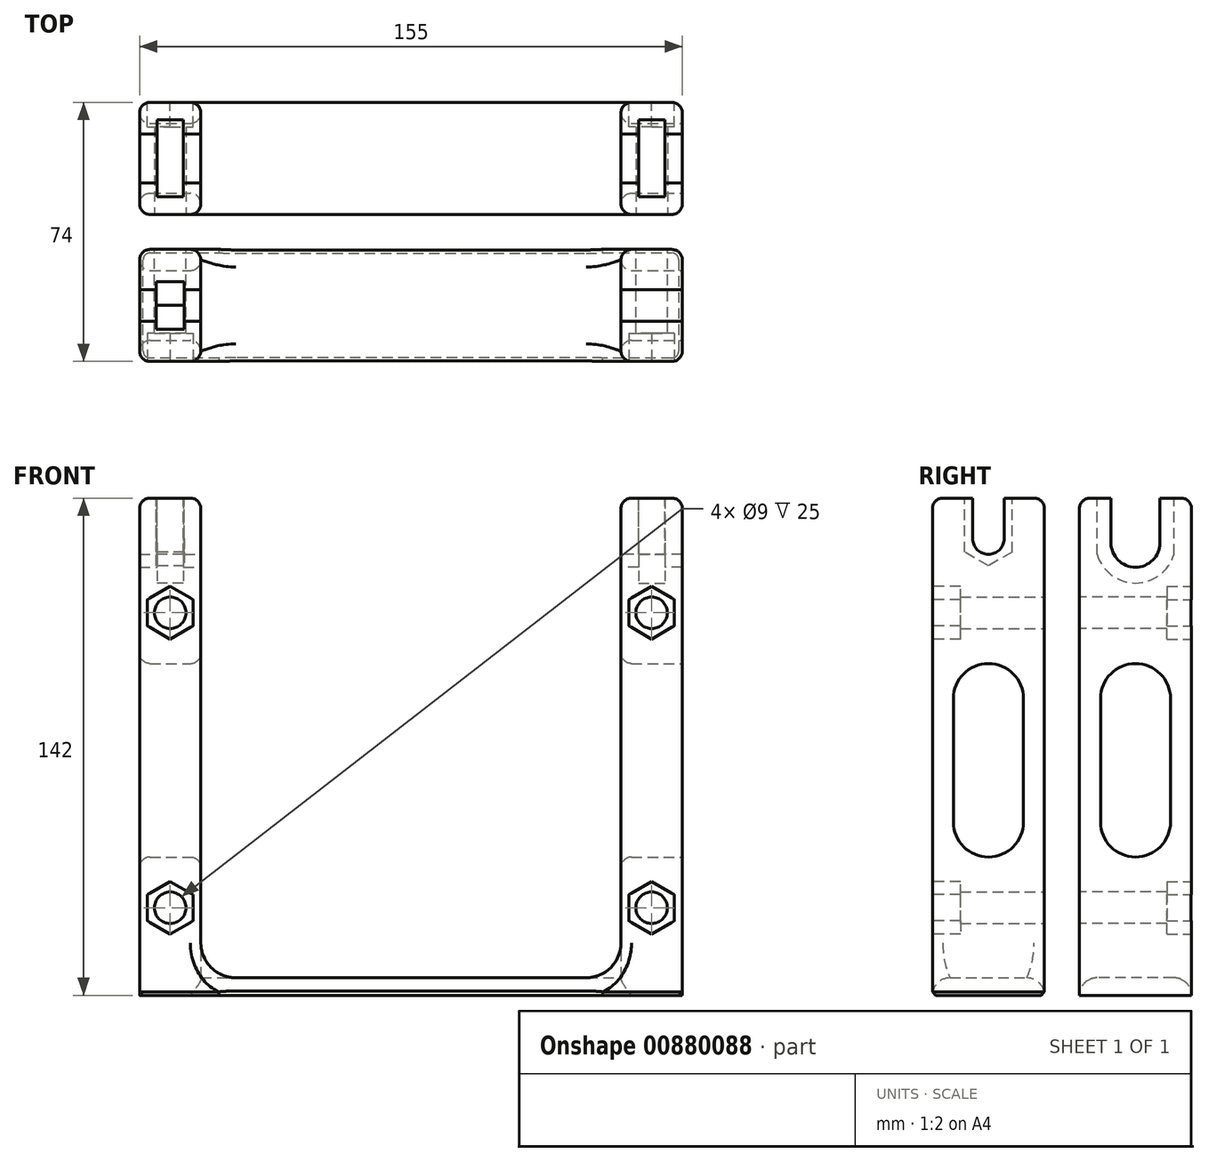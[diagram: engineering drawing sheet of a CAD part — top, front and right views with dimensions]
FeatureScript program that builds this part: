
annotation { "Feature Type Name" : "Feature", "Feature Type Description" : "" }
export const myFeature = defineFeature(function(context is Context, id is Id, definition is map)
    precondition{}
    {
        {
            var Q0;
            Q0=qCreatedBy(makeId("Top.planeOp"),FACE);
            var sketch = newSketch(context, id + "F0", { "sketchPlane" : qUnion([Q0])});
            skLineSegment(sketch, "E0.bottom", {"start": v(-77.5, 16) * mm, "end": v(-60, 16) * mm});
            skLineSegment(sketch, "E0.top", {"start": v(-77.5, -16) * mm, "end": v(-60, -16) * mm});
            skLineSegment(sketch, "E0.left", {"start": v(-77.5, 16) * mm, "end": v(-77.5, -16) * mm});
            skLineSegment(sketch, "E0.right", {"start": v(-60, 16) * mm, "end": v(-60, -16) * mm});
            skPoint(sketch, "E1", {"position": v(-60, 0) * mm});
            skSolve(sketch);
        }
        {
            var Q0;
            Q0=makeQuery(id+"F0.imprint","IMPRINT",FACE,{"disambiguationData":[TD([[makeQuery(id+"F0.imprint","IMPRINT",EDGE,{"derivedFrom":sQuery(id+"F0.wireOp",EDGE,"E0.bottom")}),-1.0]])]});
            extrude(context, id + "F1", {"entities" : qUnion([Q0]), "depth" : (22 + 5) * mm, "offsetDistance" : 25 * mm});
        }
        {
            var Q0;
            Q0=makeQuery(id+"F1.opExtrude","CAP_FACE",FACE,{"disambiguationData":[OSD([sQuery(id+"F0.wireOp",EDGE,"E0.bottom"),sQuery(id+"F0.wireOp",EDGE,"E0.top"),sQuery(id+"F0.wireOp",EDGE,"E0.left"),sQuery(id+"F0.wireOp",EDGE,"E0.right")])],"isStart":false});
            var sketch = newSketch(context, id + "F2", { "sketchPlane" : qUnion([Q0])});
            skLineSegment(sketch, "E2.bottom", {"start": v(-72.5, 11) * mm, "end": v(-65, 11) * mm});
            skLineSegment(sketch, "E2.top", {"start": v(-72.5, -11) * mm, "end": v(-65, -11) * mm});
            skLineSegment(sketch, "E2.left", {"start": v(-72.5, 11) * mm, "end": v(-72.5, -11) * mm});
            skLineSegment(sketch, "E2.right", {"start": v(-65, 11) * mm, "end": v(-65, -11) * mm});
            skPoint(sketch, "E3", {"position": v(-65, 0) * mm});
            skPoint(sketch, "E4", {"position": v(-60, 0) * mm});
            skPoint(sketch, "E5", {"position": v(-68.75, 16) * mm});
            skPoint(sketch, "E6", {"position": v(-68.75, 11) * mm});
            skSolve(sketch);
        }
        {
            var Q0;
            Q0=makeQuery(id+"F2.imprint","IMPRINT",FACE,{"disambiguationData":[TD([[makeQuery(id+"F2.imprint","IMPRINT",EDGE,{"derivedFrom":sQuery(id+"F2.wireOp",EDGE,"E2.bottom")}),-1.0]])]});
            extrude(context, id + "F3", {"entities" : qUnion([Q0]), "operationType" : NewBodyOperationType.REMOVE, "oppositeDirection" : true, "depth" : 22 * mm, "offsetDistance" : 25 * mm});
        }
        {
            var Q0;
            Q0=makeQuery(id+"F1.opExtrude","SWEPT_FACE",FACE,{"disambiguationData":[OSD([sQuery(id+"F0.wireOp",EDGE,"E0.right")])]});
            var sketch = newSketch(context, id + "F4", { "sketchPlane" : qUnion([Q0])});
            skArc(sketch, "E7", {"start": v(-7, 14.24) * mm, "mid": v(0, 7.24) * mm, "end": v(7, 14.24) * mm});
            skLineSegment(sketch, "E8", {"start": v(-7, 14.24) * mm, "end": v(-7, 27) * mm});
            skLineSegment(sketch, "E9", {"start": v(7, 27) * mm, "end": v(7, 14.24) * mm});
            skSolve(sketch);
        }
        {
            var Q0;
            Q0=makeQuery(id+"F4.imprint","IMPRINT",FACE,{"disambiguationData":[TD([[makeQuery(id+"F4.imprint","IMPRINT",EDGE,{"derivedFrom":sQuery(id+"F4.wireOp",EDGE,"E7")}),1.0]])]});
            extrude(context, id + "F5", {"entities" : qUnion([Q0]), "operationType" : NewBodyOperationType.REMOVE, "oppositeDirection" : true, "depth" : 25 * mm, "offsetDistance" : 25 * mm});
        }
        {
            var Q0;
            Q0=makeQuery(id+"F1.opExtrude","CAP_FACE",FACE,{"disambiguationData":[OSD([sQuery(id+"F0.wireOp",EDGE,"E0.bottom"),sQuery(id+"F0.wireOp",EDGE,"E0.top"),sQuery(id+"F0.wireOp",EDGE,"E0.left"),sQuery(id+"F0.wireOp",EDGE,"E0.right")])],"isStart":true});
            extrude(context, id + "F6", {"entities" : qUnion([Q0]), "operationType" : NewBodyOperationType.ADD, "depth" : 110 * mm, "offsetDistance" : 25 * mm});
        }
        {
            var Q0;
            Q0=makeQuery(id+"F3.boolean.opBoolean","COPY",FACE,{"derivedFrom":makeQuery(id+"F3.opExtrude","SWEPT_FACE",FACE,{"disambiguationData":[OSD([sQuery(id+"F2.wireOp",EDGE,"E2.left")])]})});
            var sketch = newSketch(context, id + "F7", { "sketchPlane" : qUnion([Q0])});
            skCircle(sketch, "E10", {"center": v(0, 14.24) * mm, "radius": 11.5 * mm});
            skLineSegment(sketch, "E11", {"start": v(-11, 5) * mm, "end": v(-11, 10.89) * mm});
            skLineSegment(sketch, "E12", {"start": v(-11, 5) * mm, "end": v(-6.85, 5) * mm});
            skLineSegment(sketch, "E13", {"start": v(6.85, 5) * mm, "end": v(11, 5) * mm});
            skLineSegment(sketch, "E14", {"start": v(11, 5) * mm, "end": v(11, 10.89) * mm});
            skSolve(sketch);
        }
        {
            var Q0;
            {var subQ0=sQuery(id+"F7.wireOp",EDGE,"E11");Q0=makeQuery(id+"F7.imprint","IMPRINT",FACE,{"disambiguationData":[TD([[makeQuery(id+"F7.imprint","IMPRINT",EDGE,{"derivedFrom":subQ0}),-1.0]])]});}
            var Q1;
            {var subQ0=sQuery(id+"F7.wireOp",EDGE,"E13");Q1=makeQuery(id+"F7.imprint","IMPRINT",FACE,{"disambiguationData":[TD([[makeQuery(id+"F7.imprint","IMPRINT",EDGE,{"derivedFrom":subQ0}),-1.0]])]});}
            extrude(context, id + "F8", {"entities" : qUnion([Q0, Q1]), "operationType" : NewBodyOperationType.ADD, "endBound" : BoundingType.UP_TO_NEXT, "depth" : 25 * mm, "offsetDistance" : 25 * mm});
        }
        {
            var Q0;
            {var subQ0=sQuery(id+"F7.wireOp",EDGE,"E10");var subQ1=makeQuery(id+"F3.boolean.opBoolean","COPY",EDGE,{"derivedFrom":makeQuery(id+"F3.opExtrude","CAP_EDGE",EDGE,{"disambiguationData":[OSD([sQuery(id+"F2.wireOp",EDGE,"E2.left")])],"isStart":false})});var subQ2=makeQuery(id+"F7.imprint","INTERSECT",VERTEX,{"derivedFrom":[subQ1,subQ0,sQuery(id+"F7.wireOp",EDGE,"E12")]});Q0=makeQuery(id+"F7.imprint","IMPRINT",FACE,{"disambiguationData":[TD([[makeQuery(id+"F7.imprint","IMPRINT",EDGE,{"disambiguationData":[TD([[subQ2,-1.0]])],"derivedFrom":subQ0}),1.0]])]});}
            var Q1;
            Q1=makeQuery(id+"F3.boolean.opBoolean","COPY",FACE,{"derivedFrom":makeQuery(id+"F3.opExtrude","SWEPT_FACE",FACE,{"disambiguationData":[OSD([sQuery(id+"F2.wireOp",EDGE,"E2.right")])]})});
            extrude(context, id + "F9", {"entities" : qUnion([Q0]), "operationType" : NewBodyOperationType.REMOVE, "endBound" : BoundingType.UP_TO_SURFACE, "depth" : 25 * mm, "endBoundEntityFace" : qUnion([Q1]), "offsetDistance" : 25 * mm});
        }
        {
            var Q0;
            Q0=makeQuery(id+"F6.opExtrude","CAP_FACE",FACE,{"disambiguationData":[OSD([sQuery(id+"F0.wireOp",EDGE,"E0.bottom"),sQuery(id+"F0.wireOp",EDGE,"E0.top"),sQuery(id+"F0.wireOp",EDGE,"E0.left"),sQuery(id+"F0.wireOp",EDGE,"E0.right")])],"isStart":false});
            var sketch = newSketch(context, id + "F10", { "sketchPlane" : qUnion([Q0])});
            skLineSegment(sketch, "E15.bottom", {"start": v(-60, 16) * mm, "end": v(0, 16) * mm});
            skLineSegment(sketch, "E15.top", {"start": v(-60, -16) * mm, "end": v(0, -16) * mm});
            skLineSegment(sketch, "E15.left", {"start": v(-60, 16) * mm, "end": v(-60, -16) * mm});
            skLineSegment(sketch, "E15.right", {"start": v(0, 16) * mm, "end": v(0, -16) * mm});
            skSolve(sketch);
        }
        {
            var Q0;
            Q0=makeQuery(id+"F10.imprint","IMPRINT",FACE,{"disambiguationData":[TD([[makeQuery(id+"F10.imprint","IMPRINT",EDGE,{"derivedFrom":sQuery(id+"F10.wireOp",EDGE,"E15.bottom")}),-1.0]])]});
            var Q1;
            Q1=makeQuery(id+"F10.imprint","IMPRINT",FACE,{"disambiguationData":[TD([[makeQuery(id+"F10.imprint","IMPRINT",EDGE,{"derivedFrom":sQuery(id+"F10.wireOp",EDGE,"E15.left")}),1.0]])]});
            extrude(context, id + "F11", {"entities" : qUnion([Q0, Q1]), "operationType" : NewBodyOperationType.ADD, "depth" : 5 * mm, "offsetDistance" : 25 * mm});
        }
        {
            var Q0;
            {var subQ0=sQuery(id+"F0.wireOp",EDGE,"E0.top");var subQ1=makeQuery(id+"F11.boolean.opBoolean","MERGE",FACE,{"derivedFrom":[makeQuery(id+"F6.boolean.opBoolean","MERGE",FACE,{"derivedFrom":[makeQuery(id+"F1.opExtrude","SWEPT_FACE",FACE,{"disambiguationData":[OSD([subQ0])]}),makeQuery(id+"F6.opExtrude","SWEPT_FACE",FACE,{"disambiguationData":[OSD([subQ0])]})]}),makeQuery(id+"F11.opExtrude","SWEPT_FACE",FACE,{"disambiguationData":[OSD([subQ0,sQuery(id+"F10.wireOp",EDGE,"E15.bottom")])]})]});Q0=makeQuery(id+"F16.boolean.opBoolean","MERGE",FACE,{"derivedFrom":[subQ1,makeQuery(id+"F16.opPattern","COPY",FACE,{"derivedFrom":subQ1,"instanceName":"1"})]});}
            var sketch = newSketch(context, id + "F12", { "sketchPlane" : qUnion([Q0])});
            skPoint(sketch, "E16", {"position": v(-68.75, -5.76) * mm});
            skLineSegment(sketch, "E17", {"start": v(-68.75, -5.76) * mm, "end": v(-77.5, -5.76) * mm, "construction": true});
            skLineSegment(sketch, "E18", {"start": v(-68.75, -5.76) * mm, "end": v(-60, -5.76) * mm, "construction": true});
            skPoint(sketch, "E19", {"position": v(-68.75, -90) * mm});
            skSolve(sketch);
        }
        {
            var Q0;
            Q0=sQuery(id+"F12.wireOp",VERTEX,"E19");
            var Q1;
            Q1=sQuery(id+"F12.wireOp",VERTEX,"E16");
            var Q2;
            Q2=makeQuery(id+"F1.opExtrude","SWEPT_BODY",BODY,{"disambiguationData":[OSD([sQuery(id+"F0.wireOp",EDGE,"E0.bottom"),sQuery(id+"F0.wireOp",EDGE,"E0.top"),sQuery(id+"F0.wireOp",EDGE,"E0.left"),sQuery(id+"F0.wireOp",EDGE,"E0.right")])]});
            hole(context, id + "F13", {"style" : HoleStyle.SIMPLE, "endStyle" : HoleEndStyle.THROUGH, "standardTappedOrClearance" : lookupTablePath({ "fit" : "Normal", "standard" : "ISO", "size" : "M8", "type" : "Clearance" }), "standardBlindInLast" : lookupTablePath({ "fit" : "Normal", "standard" : "ISO", "engagement" : "75%", "pitch" : "1.25 mm", "size" : "M8", "type" : "Clearance & tapped" }), "holeDiameter" : 9 * mm, "majorDiameter" : 5 * mm, "isTappedThrough" : true, "tappedDepth" : 8.5 * mm, "tapClearance" : 3, "startFromSketch" : true, "locations" : qUnion([Q0, Q1]), "scope" : qUnion([Q2])});
        }
        {
            var Q0;
            {var subQ0=sQuery(id+"F0.wireOp",EDGE,"E0.bottom");var subQ1=makeQuery(id+"F11.boolean.opBoolean","MERGE",FACE,{"derivedFrom":[makeQuery(id+"F6.boolean.opBoolean","MERGE",FACE,{"derivedFrom":[makeQuery(id+"F1.opExtrude","SWEPT_FACE",FACE,{"disambiguationData":[OSD([subQ0])]}),makeQuery(id+"F6.opExtrude","SWEPT_FACE",FACE,{"disambiguationData":[OSD([subQ0])]})]}),makeQuery(id+"F11.opExtrude","SWEPT_FACE",FACE,{"disambiguationData":[OSD([subQ0,sQuery(id+"F10.wireOp",EDGE,"E15.top")])]})]});Q0=makeQuery(id+"F16.boolean.opBoolean","MERGE",FACE,{"derivedFrom":[subQ1,makeQuery(id+"F16.opPattern","COPY",FACE,{"derivedFrom":subQ1,"instanceName":"1"})]});}
            var sketch = newSketch(context, id + "F14", { "sketchPlane" : qUnion([Q0])});
            skCircle(sketch, "E20.cCircle", {"center": v(68.75, -5.76) * mm, "radius": 6.5 * mm, "construction": true});
            skLineSegment(sketch, "E20.0", {"start": v(62.25, -9.51) * mm, "end": v(62.25, -2) * mm});
            skLineSegment(sketch, "E20.1", {"start": v(62.25, -2) * mm, "end": v(68.75, 1.75) * mm});
            skLineSegment(sketch, "E20.2", {"start": v(68.75, 1.75) * mm, "end": v(75.25, -2) * mm});
            skLineSegment(sketch, "E20.3", {"start": v(75.25, -2) * mm, "end": v(75.25, -9.51) * mm});
            skLineSegment(sketch, "E20.4", {"start": v(75.25, -9.51) * mm, "end": v(68.75, -13.26) * mm});
            skLineSegment(sketch, "E20.5", {"start": v(68.75, -13.26) * mm, "end": v(62.25, -9.51) * mm});
            skPoint(sketch, "E20.0.midPoint", {"position": v(62.25, -5.76) * mm});
            skCircle(sketch, "E21.cCircle", {"center": v(68.75, -90) * mm, "radius": 6.5 * mm, "construction": true});
            skLineSegment(sketch, "E21.0", {"start": v(62.25, -93.75) * mm, "end": v(62.25, -86.25) * mm});
            skLineSegment(sketch, "E21.1", {"start": v(62.25, -86.25) * mm, "end": v(68.75, -82.5) * mm});
            skLineSegment(sketch, "E21.2", {"start": v(68.75, -82.5) * mm, "end": v(75.25, -86.25) * mm});
            skLineSegment(sketch, "E21.3", {"start": v(75.25, -86.25) * mm, "end": v(75.25, -93.75) * mm});
            skLineSegment(sketch, "E21.4", {"start": v(75.25, -93.75) * mm, "end": v(68.75, -97.5) * mm});
            skLineSegment(sketch, "E21.5", {"start": v(68.75, -97.5) * mm, "end": v(62.25, -93.75) * mm});
            skPoint(sketch, "E21.0.midPoint", {"position": v(62.25, -90) * mm});
            skSolve(sketch);
        }
        {
            var Q0;
            Q0=makeQuery(id+"F14.imprint","IMPRINT",FACE,{"disambiguationData":[TD([[makeQuery(id+"F14.imprint","IMPRINT",EDGE,{"derivedFrom":sQuery(id+"F14.wireOp",EDGE,"E20.0")}),-1.0]])]});
            var Q1;
            Q1=makeQuery(id+"F14.imprint","IMPRINT",FACE,{"disambiguationData":[TD([[makeQuery(id+"F14.imprint","IMPRINT",EDGE,{"derivedFrom":sQuery(id+"F14.wireOp",EDGE,"E21.0")}),-1.0]])]});
            extrude(context, id + "F15", {"entities" : qUnion([Q0, Q1]), "operationType" : NewBodyOperationType.REMOVE, "oppositeDirection" : true, "depth" : 7 * mm, "offsetDistance" : 25 * mm});
        }
        {
            var Q0;
            Q0=makeQuery(id+"F1.opExtrude","SWEPT_BODY",BODY,{"disambiguationData":[OSD([sQuery(id+"F0.wireOp",EDGE,"E0.bottom"),sQuery(id+"F0.wireOp",EDGE,"E0.top"),sQuery(id+"F0.wireOp",EDGE,"E0.left"),sQuery(id+"F0.wireOp",EDGE,"E0.right")])]});
            var Q1;
            Q1=qCreatedBy(makeId("Right.planeOp"),FACE);
            mirror(context, id + "F16", {"operationType" : NewBodyOperationType.ADD, "entities" : qUnion([Q0]), "mirrorPlane" : qUnion([Q1])});
        }
        {
            var Q0;
            {var subQ0=sQuery(id+"F0.wireOp",EDGE,"E0.top");var subQ1=makeQuery(id+"F11.boolean.opBoolean","MERGE",FACE,{"derivedFrom":[makeQuery(id+"F6.boolean.opBoolean","MERGE",FACE,{"derivedFrom":[makeQuery(id+"F1.opExtrude","SWEPT_FACE",FACE,{"disambiguationData":[OSD([subQ0])]}),makeQuery(id+"F6.opExtrude","SWEPT_FACE",FACE,{"disambiguationData":[OSD([subQ0])]})]}),makeQuery(id+"F11.opExtrude","SWEPT_FACE",FACE,{"disambiguationData":[OSD([subQ0,sQuery(id+"F10.wireOp",EDGE,"E15.bottom")])]})]});Q0=makeQuery(id+"F16.boolean.opBoolean","MERGE",FACE,{"derivedFrom":[subQ1,makeQuery(id+"F16.opPattern","COPY",FACE,{"derivedFrom":subQ1,"instanceName":"1"})]});}
            cPlane(context, id + "F17", {"entities" : qUnion([Q0]), "cplaneType" : CPlaneType.OFFSET, "offset" : 10 * mm, "width" : 150 * mm, "height" : 150 * mm});
        }
        {
            var Q0;
            Q0=qCreatedBy(id+"F17.planeOp",FACE);
            var sketch = newSketch(context, id + "F18", { "sketchPlane" : qUnion([Q0])});
            skLineSegment(sketch, "E22.0", {"start": v(-77.5, 27) * mm, "end": v(-77.5, -115) * mm});
            skLineSegment(sketch, "E22.1", {"start": v(-60, 27) * mm, "end": v(-60, -110) * mm});
            skLineSegment(sketch, "E22.2", {"start": v(-77.5, 27) * mm, "end": v(-60, 27) * mm});
            skCircle(sketch, "E22.3", {"center": v(-68.75, -5.76) * mm, "radius": 4.5 * mm});
            skCircle(sketch, "E22.4", {"center": v(-68.75, -90) * mm, "radius": 4.5 * mm});
            skLineSegment(sketch, "E22.5", {"start": v(-77.5, -115) * mm, "end": v(77.5, -115) * mm});
            skLineSegment(sketch, "E22.6", {"start": v(-60, -110) * mm, "end": v(60, -110) * mm});
            skLineSegment(sketch, "E22.7", {"start": v(60, 27) * mm, "end": v(60, -110) * mm});
            skLineSegment(sketch, "E22.8", {"start": v(77.5, 27) * mm, "end": v(77.5, -115) * mm});
            skCircle(sketch, "E22.9", {"center": v(68.75, -90) * mm, "radius": 4.5 * mm});
            skCircle(sketch, "E22.10", {"center": v(68.75, -5.76) * mm, "radius": 4.5 * mm});
            skLineSegment(sketch, "E22.11", {"start": v(77.5, 27) * mm, "end": v(60, 27) * mm});
            skSolve(sketch);
        }
        {
            var Q0;
            Q0=makeQuery(id+"F18.imprint","IMPRINT",FACE,{"disambiguationData":[TD([[makeQuery(id+"F18.imprint","IMPRINT",EDGE,{"derivedFrom":sQuery(id+"F18.wireOp",EDGE,"E22.0")}),1.0]])]});
            extrude(context, id + "F19", {"entities" : qUnion([Q0]), "depth" : 32 * mm, "offsetDistance" : 25 * mm});
        }
        {
            var Q0;
            Q0=makeQuery(id+"F19.opExtrude","SWEPT_FACE",FACE,{"disambiguationData":[OSD([sQuery(id+"F18.wireOp",EDGE,"E22.1")])]});
            var sketch = newSketch(context, id + "F20", { "sketchPlane" : qUnion([Q0])});
            skLineSegment(sketch, "E23", {"start": v(-46.5, 27) * mm, "end": v(-37.5, 27) * mm});
            skLineSegment(sketch, "E24", {"start": v(-46.5, 27) * mm, "end": v(-46.5, 15.45) * mm});
            skLineSegment(sketch, "E25", {"start": v(-46.5, 15.45) * mm, "end": v(-37.5, 15.45) * mm});
            skLineSegment(sketch, "E26", {"start": v(-37.5, 15.45) * mm, "end": v(-37.5, 27) * mm});
            skPoint(sketch, "E27", {"position": v(-42, 15.45) * mm});
            skPoint(sketch, "E28", {"position": v(-42, 27) * mm});
            skCircle(sketch, "E29", {"center": v(-42, 15.45) * mm, "radius": 4.5 * mm});
            skSolve(sketch);
        }
        {
            var Q0;
            Q0=makeQuery(id+"F20.imprint","IMPRINT",FACE,{"disambiguationData":[TD([[makeQuery(id+"F20.imprint","IMPRINT",EDGE,{"derivedFrom":sQuery(id+"F20.wireOp",EDGE,"E23")}),-1.0]])]});
            var Q1;
            {var subQ0=sQuery(id+"F20.wireOp",EDGE,"E25");Q1=makeQuery(id+"F20.imprint","IMPRINT",FACE,{"disambiguationData":[TD([[makeQuery(id+"F20.imprint","IMPRINT",EDGE,{"derivedFrom":subQ0}),-1.0]])]});}
            var Q2;
            {var subQ0=sQuery(id+"F20.wireOp",EDGE,"E25");Q2=makeQuery(id+"F20.imprint","IMPRINT",FACE,{"disambiguationData":[TD([[makeQuery(id+"F20.imprint","IMPRINT",EDGE,{"derivedFrom":subQ0}),1.0]])]});}
            extrude(context, id + "F21", {"entities" : qUnion([Q0, Q1, Q2]), "operationType" : NewBodyOperationType.REMOVE, "oppositeDirection" : true, "depth" : 25 * mm, "offsetDistance" : 25 * mm});
        }
        {
            var Q0;
            {var subQ1=sQuery(id+"F18.wireOp",EDGE,"E22.2");Q0=makeQuery(id+"F21.boolean.opBoolean","SPLIT",FACE,{"disambiguationData":[TD([makeQuery(id+"F21.opExtrude","SWEPT_FACE",FACE,{"disambiguationData":[OSD([sQuery(id+"F20.wireOp",EDGE,"E24")])]})])],"derivedFrom":makeQuery(id+"F19.opExtrude","SWEPT_FACE",FACE,{"disambiguationData":[OSD([subQ1])]})});}
            var sketch = newSketch(context, id + "F22", { "sketchPlane" : qUnion([Q0])});
            skLineSegment(sketch, "E30.bottom", {"start": v(-72.75, -48.75) * mm, "end": v(-64.75, -48.75) * mm});
            skLineSegment(sketch, "E30.top", {"start": v(-72.75, -35.25) * mm, "end": v(-64.75, -35.25) * mm});
            skLineSegment(sketch, "E30.left", {"start": v(-72.75, -48.75) * mm, "end": v(-72.75, -35.25) * mm});
            skLineSegment(sketch, "E30.right", {"start": v(-64.75, -48.75) * mm, "end": v(-64.75, -35.25) * mm});
            skPoint(sketch, "E31", {"position": v(-68.75, -48.75) * mm});
            skPoint(sketch, "E32", {"position": v(-68.75, -58) * mm});
            skLineSegment(sketch, "E33", {"start": v(-60, -46.5) * mm, "end": v(-60, -37.5) * mm, "construction": true});
            skPoint(sketch, "E34", {"position": v(-60, -42) * mm});
            skPoint(sketch, "E35", {"position": v(-64.75, -42) * mm});
            skSolve(sketch);
        }
        {
            var Q0;
            {var subQ0=sQuery(id+"F22.wireOp",EDGE,"E30.top");Q0=makeQuery(id+"F22.imprint","IMPRINT",FACE,{"disambiguationData":[TD([[makeQuery(id+"F22.imprint","IMPRINT",EDGE,{"derivedFrom":subQ0}),-1.0]])]});}
            var Q1;
            {var subQ0=sQuery(id+"F22.wireOp",EDGE,"E30.bottom");Q1=makeQuery(id+"F22.imprint","IMPRINT",FACE,{"disambiguationData":[TD([[makeQuery(id+"F22.imprint","IMPRINT",EDGE,{"derivedFrom":subQ0}),1.0]])]});}
            extrude(context, id + "F23", {"entities" : qUnion([Q0, Q1]), "operationType" : NewBodyOperationType.REMOVE, "oppositeDirection" : true, "depth" : 11.8 * mm, "offsetDistance" : 25 * mm});
        }
        {
            var Q0;
            {var subQ1=sQuery(id+"F22.wireOp",EDGE,"E30.left");Q0=makeQuery(id+"F23.boolean.opBoolean","COPY",FACE,{"disambiguationData":[TD([makeQuery(id+"F21.boolean.opBoolean","COPY",FACE,{"derivedFrom":makeQuery(id+"F21.opExtrude","SWEPT_FACE",FACE,{"disambiguationData":[OSD([sQuery(id+"F20.wireOp",EDGE,"E24")])]})})])],"derivedFrom":makeQuery(id+"F23.opExtrude","SWEPT_FACE",FACE,{"disambiguationData":[OSD([subQ1])]})});}
            var sketch = newSketch(context, id + "F24", { "sketchPlane" : qUnion([Q0])});
            skCircle(sketch, "E36.cCircle", {"center": v(-42, 15.45) * mm, "radius": 6.75 * mm, "construction": true});
            skLineSegment(sketch, "E36.0", {"start": v(-35.25, 19.34) * mm, "end": v(-35.25, 11.55) * mm});
            skLineSegment(sketch, "E36.1", {"start": v(-35.25, 11.55) * mm, "end": v(-42, 7.65) * mm});
            skLineSegment(sketch, "E36.2", {"start": v(-42, 7.65) * mm, "end": v(-48.75, 11.55) * mm});
            skLineSegment(sketch, "E36.3", {"start": v(-48.75, 11.55) * mm, "end": v(-48.75, 19.34) * mm});
            skLineSegment(sketch, "E36.4", {"start": v(-48.75, 19.34) * mm, "end": v(-42, 23.24) * mm});
            skLineSegment(sketch, "E36.5", {"start": v(-42, 23.24) * mm, "end": v(-35.25, 19.34) * mm});
            skPoint(sketch, "E36.0.midPoint", {"position": v(-35.25, 15.45) * mm});
            skSolve(sketch);
        }
        {
            var Q0;
            Q0=makeQuery(id+"F24.imprint","IMPRINT",FACE,{"disambiguationData":[TD([[makeQuery(id+"F24.imprint","IMPRINT",EDGE,{"derivedFrom":sQuery(id+"F24.wireOp",EDGE,"E36.0")}),-1.0]])]});
            var Q1;
            {var subQ1=sQuery(id+"F22.wireOp",EDGE,"E30.right");Q1=makeQuery(id+"F23.boolean.opBoolean","COPY",FACE,{"disambiguationData":[TD([makeQuery(id+"F21.boolean.opBoolean","COPY",FACE,{"derivedFrom":makeQuery(id+"F21.opExtrude","SWEPT_FACE",FACE,{"disambiguationData":[OSD([sQuery(id+"F20.wireOp",EDGE,"E24")])]})})])],"derivedFrom":makeQuery(id+"F23.opExtrude","SWEPT_FACE",FACE,{"disambiguationData":[OSD([subQ1])]})});}
            extrude(context, id + "F25", {"entities" : qUnion([Q0]), "operationType" : NewBodyOperationType.REMOVE, "endBound" : BoundingType.UP_TO_SURFACE, "depth" : 25 * mm, "endBoundEntityFace" : qUnion([Q1]), "offsetDistance" : 25 * mm});
        }
        {
            var Q0;
            Q0=makeQuery(id+"F19.opExtrude","SWEPT_FACE",FACE,{"disambiguationData":[OSD([sQuery(id+"F18.wireOp",EDGE,"E22.7")])]});
            var sketch = newSketch(context, id + "F26", { "sketchPlane" : qUnion([Q0])});
            skLineSegment(sketch, "E37.0", {"start": v(37.5, 15.45) * mm, "end": v(37.5, 27) * mm});
            skArc(sketch, "E37.1", {"start": v(46.5, 15.45) * mm, "mid": v(42, 10.95) * mm, "end": v(37.5, 15.45) * mm});
            skLineSegment(sketch, "E37.2", {"start": v(46.5, 27) * mm, "end": v(46.5, 15.45) * mm});
            skSolve(sketch);
        }
        {
            var Q0;
            {var subQ0=sQuery(id+"F26.wireOp",EDGE,"E37.0");Q0=makeQuery(id+"F26.imprint","IMPRINT",FACE,{"disambiguationData":[TD([[makeQuery(id+"F26.imprint","IMPRINT",EDGE,{"derivedFrom":subQ0}),-1.0]])]});}
            extrude(context, id + "F27", {"entities" : qUnion([Q0]), "operationType" : NewBodyOperationType.REMOVE, "endBound" : BoundingType.THROUGH_ALL, "oppositeDirection" : true, "depth" : 25 * mm, "offsetDistance" : 25 * mm});
        }
        {
            var Q0;
            Q0=makeQuery(id+"F19.opExtrude","CAP_FACE",FACE,{"disambiguationData":[OSD([sQuery(id+"F18.wireOp",EDGE,"E22.0"),sQuery(id+"F18.wireOp",EDGE,"E22.1"),sQuery(id+"F18.wireOp",EDGE,"E22.2"),sQuery(id+"F18.wireOp",EDGE,"E22.3"),sQuery(id+"F18.wireOp",EDGE,"E22.4"),sQuery(id+"F18.wireOp",EDGE,"E22.5"),sQuery(id+"F18.wireOp",EDGE,"E22.6"),sQuery(id+"F18.wireOp",EDGE,"E22.7"),sQuery(id+"F18.wireOp",EDGE,"E22.8"),sQuery(id+"F18.wireOp",EDGE,"E22.9"),sQuery(id+"F18.wireOp",EDGE,"E22.10"),sQuery(id+"F18.wireOp",EDGE,"E22.11")])],"isStart":false});
            var sketch = newSketch(context, id + "F28", { "sketchPlane" : qUnion([Q0])});
            skLineSegment(sketch, "E38.0", {"start": v(75.25, -93.75) * mm, "end": v(68.75, -97.5) * mm});
            skLineSegment(sketch, "E38.1", {"start": v(75.25, -86.25) * mm, "end": v(75.25, -93.75) * mm});
            skLineSegment(sketch, "E38.2", {"start": v(68.75, -82.5) * mm, "end": v(75.25, -86.25) * mm});
            skLineSegment(sketch, "E38.3", {"start": v(62.25, -86.25) * mm, "end": v(68.75, -82.5) * mm});
            skLineSegment(sketch, "E38.4", {"start": v(62.25, -93.75) * mm, "end": v(62.25, -86.25) * mm});
            skLineSegment(sketch, "E38.5", {"start": v(68.75, -97.5) * mm, "end": v(62.25, -93.75) * mm});
            skLineSegment(sketch, "E38.6", {"start": v(75.25, -9.51) * mm, "end": v(68.75, -13.26) * mm});
            skLineSegment(sketch, "E38.7", {"start": v(75.25, -2) * mm, "end": v(75.25, -9.51) * mm});
            skLineSegment(sketch, "E38.8", {"start": v(68.75, 1.75) * mm, "end": v(75.25, -2) * mm});
            skLineSegment(sketch, "E38.9", {"start": v(62.25, -2) * mm, "end": v(68.75, 1.75) * mm});
            skLineSegment(sketch, "E38.10", {"start": v(62.25, -9.51) * mm, "end": v(62.25, -2) * mm});
            skLineSegment(sketch, "E38.11", {"start": v(68.75, -13.26) * mm, "end": v(62.25, -9.51) * mm});
            skLineSegment(sketch, "E38.12", {"start": v(-68.75, -97.5) * mm, "end": v(-62.25, -93.75) * mm});
            skLineSegment(sketch, "E38.13", {"start": v(-75.25, -93.75) * mm, "end": v(-68.75, -97.5) * mm});
            skLineSegment(sketch, "E38.14", {"start": v(-75.25, -86.25) * mm, "end": v(-75.25, -93.75) * mm});
            skLineSegment(sketch, "E38.15", {"start": v(-68.75, -82.5) * mm, "end": v(-75.25, -86.25) * mm});
            skLineSegment(sketch, "E38.16", {"start": v(-62.25, -86.25) * mm, "end": v(-68.75, -82.5) * mm});
            skLineSegment(sketch, "E38.17", {"start": v(-62.25, -93.75) * mm, "end": v(-62.25, -86.25) * mm});
            skLineSegment(sketch, "E38.18", {"start": v(-62.25, -9.51) * mm, "end": v(-62.25, -2) * mm});
            skLineSegment(sketch, "E38.19", {"start": v(-68.75, -13.26) * mm, "end": v(-62.25, -9.51) * mm});
            skLineSegment(sketch, "E38.20", {"start": v(-75.25, -9.51) * mm, "end": v(-68.75, -13.26) * mm});
            skLineSegment(sketch, "E38.21", {"start": v(-75.25, -2) * mm, "end": v(-75.25, -9.51) * mm});
            skLineSegment(sketch, "E38.22", {"start": v(-68.75, 1.75) * mm, "end": v(-75.25, -2) * mm});
            skLineSegment(sketch, "E38.23", {"start": v(-62.25, -2) * mm, "end": v(-68.75, 1.75) * mm});
            skSolve(sketch);
        }
        {
            var Q0;
            Q0=makeQuery(id+"F28.imprint","IMPRINT",FACE,{"disambiguationData":[TD([[makeQuery(id+"F28.imprint","IMPRINT",EDGE,{"derivedFrom":sQuery(id+"F28.wireOp",EDGE,"E38.18")}),1.0]])]});
            var Q1;
            Q1=makeQuery(id+"F28.imprint","IMPRINT",FACE,{"disambiguationData":[TD([[makeQuery(id+"F28.imprint","IMPRINT",EDGE,{"derivedFrom":sQuery(id+"F28.wireOp",EDGE,"E38.12")}),1.0]])]});
            var Q2;
            Q2=makeQuery(id+"F28.imprint","IMPRINT",FACE,{"disambiguationData":[TD([[makeQuery(id+"F28.imprint","IMPRINT",EDGE,{"derivedFrom":sQuery(id+"F28.wireOp",EDGE,"E38.0")}),-1.0]])]});
            var Q3;
            Q3=makeQuery(id+"F28.imprint","IMPRINT",FACE,{"disambiguationData":[TD([[makeQuery(id+"F28.imprint","IMPRINT",EDGE,{"derivedFrom":sQuery(id+"F28.wireOp",EDGE,"E38.6")}),-1.0]])]});
            extrude(context, id + "F29", {"entities" : qUnion([Q0, Q1, Q2, Q3]), "operationType" : NewBodyOperationType.REMOVE, "oppositeDirection" : true, "depth" : 8 * mm, "offsetDistance" : 25 * mm});
        }
        {
            var Q0;
            Q0=makeQuery(id+"F29.boolean.opBoolean","COPY",FACE,{"derivedFrom":makeQuery(id+"F29.opExtrude","CAP_FACE",FACE,{"disambiguationData":[OSD([sQuery(id+"F18.wireOp",EDGE,"E22.10"),sQuery(id+"F28.wireOp",EDGE,"E38.6"),sQuery(id+"F28.wireOp",EDGE,"E38.7"),sQuery(id+"F28.wireOp",EDGE,"E38.8"),sQuery(id+"F28.wireOp",EDGE,"E38.9"),sQuery(id+"F28.wireOp",EDGE,"E38.10"),sQuery(id+"F28.wireOp",EDGE,"E38.11")])],"isStart":false})});
            var sketch = newSketch(context, id + "F30", { "sketchPlane" : qUnion([Q0])});
            skPoint(sketch, "E39", {"position": v(68.75, -10.26) * mm});
            skPoint(sketch, "E40", {"position": v(68.75, -5.76) * mm});
            skPoint(sketch, "E41", {"position": v(68.75, -85.5) * mm});
            skSolve(sketch);
        }
        {
            var Q0;
            Q0=makeQuery(id+"F19.opExtrude","SWEPT_FACE",FACE,{"disambiguationData":[OSD([sQuery(id+"F18.wireOp",EDGE,"E22.8")])]});
            var sketch = newSketch(context, id + "F31", { "sketchPlane" : qUnion([Q0])});
            skArc(sketch, "E42", {"start": v(-32, -30.26) * mm, "mid": v(-42, -20.26) * mm, "end": v(-52, -30.26) * mm});
            skPoint(sketch, "E43", {"position": v(-42, -20.26) * mm});
            skArc(sketch, "E44", {"start": v(-52, -65.5) * mm, "mid": v(-42, -75.5) * mm, "end": v(-32, -65.5) * mm});
            skPoint(sketch, "E45", {"position": v(-42, -75.5) * mm});
            skLineSegment(sketch, "E46", {"start": v(-52, -65.5) * mm, "end": v(-52, -30.26) * mm});
            skLineSegment(sketch, "E47", {"start": v(-32, -30.26) * mm, "end": v(-32, -65.5) * mm});
            skArc(sketch, "E48", {"start": v(10, -30.26) * mm, "mid": v(0, -20.26) * mm, "end": v(-10, -30.26) * mm});
            skPoint(sketch, "E49", {"position": v(0, -20.26) * mm});
            skArc(sketch, "E50", {"start": v(-10, -65.5) * mm, "mid": v(0, -75.5) * mm, "end": v(10, -65.5) * mm});
            skPoint(sketch, "E51", {"position": v(0, -75.5) * mm});
            skLineSegment(sketch, "E52", {"start": v(-10, -65.5) * mm, "end": v(-10, -30.26) * mm});
            skLineSegment(sketch, "E53", {"start": v(10, -30.26) * mm, "end": v(10, -65.5) * mm});
            skSolve(sketch);
        }
        {
            var Q0;
            Q0=makeQuery(id+"F31.imprint","IMPRINT",FACE,{"disambiguationData":[TD([[makeQuery(id+"F31.imprint","IMPRINT",EDGE,{"derivedFrom":sQuery(id+"F31.wireOp",EDGE,"E42")}),1.0]])]});
            var Q1;
            Q1=makeQuery(id+"F31.imprint","IMPRINT",FACE,{"disambiguationData":[TD([[makeQuery(id+"F31.imprint","IMPRINT",EDGE,{"derivedFrom":sQuery(id+"F31.wireOp",EDGE,"E48")}),1.0]])]});
            extrude(context, id + "F32", {"entities" : qUnion([Q0, Q1]), "operationType" : NewBodyOperationType.REMOVE, "endBound" : BoundingType.THROUGH_ALL, "oppositeDirection" : true, "depth" : 25 * mm, "offsetDistance" : 25 * mm});
        }
        {
            var Q0;
            Q0=makeQuery(id+"F19.opExtrude","CAP_EDGE",EDGE,{"disambiguationData":[OSD([sQuery(id+"F18.wireOp",EDGE,"E22.1")])],"isStart":true});
            var Q1;
            Q1=makeQuery(id+"F19.opExtrude","CAP_EDGE",EDGE,{"disambiguationData":[OSD([sQuery(id+"F18.wireOp",EDGE,"E22.0")])],"isStart":true});
            var Q2;
            Q2=makeQuery(id+"F19.opExtrude","CAP_EDGE",EDGE,{"disambiguationData":[OSD([sQuery(id+"F18.wireOp",EDGE,"E22.8")])],"isStart":true});
            var Q3;
            Q3=makeQuery(id+"F19.opExtrude","CAP_EDGE",EDGE,{"disambiguationData":[OSD([sQuery(id+"F18.wireOp",EDGE,"E22.7")])],"isStart":true});
            var Q4;
            Q4=makeQuery(id+"F19.opExtrude","CAP_EDGE",EDGE,{"disambiguationData":[OSD([sQuery(id+"F18.wireOp",EDGE,"E22.8")])],"isStart":false});
            var Q5;
            Q5=makeQuery(id+"F19.opExtrude","CAP_EDGE",EDGE,{"disambiguationData":[OSD([sQuery(id+"F18.wireOp",EDGE,"E22.7")])],"isStart":false});
            var Q6;
            Q6=makeQuery(id+"F19.opExtrude","CAP_EDGE",EDGE,{"disambiguationData":[OSD([sQuery(id+"F18.wireOp",EDGE,"E22.1")])],"isStart":false});
            var Q7;
            Q7=makeQuery(id+"F19.opExtrude","CAP_EDGE",EDGE,{"disambiguationData":[OSD([sQuery(id+"F18.wireOp",EDGE,"E22.0")])],"isStart":false});
            var Q8;
            Q8=makeQuery(id+"F19.opExtrude","CAP_EDGE",EDGE,{"disambiguationData":[OSD([sQuery(id+"F18.wireOp",EDGE,"E22.2")])],"isStart":false});
            var Q9;
            {var subQ0=sQuery(id+"F18.wireOp",EDGE,"E22.2");var subQ1=sQuery(id+"F18.wireOp",EDGE,"E22.1");Q9=makeQuery(id+"F21.boolean.opBoolean","SPLIT",EDGE,{"disambiguationData":[TD([makeQuery(id+"F21.opExtrude","SWEPT_FACE",FACE,{"disambiguationData":[OSD([sQuery(id+"F20.wireOp",EDGE,"E24")])]})])],"derivedFrom":makeQuery(id+"F19.opExtrude","SWEPT_EDGE",EDGE,{"disambiguationData":[OSD([subQ1,subQ0])]})});}
            var Q10;
            {var subQ0=sQuery(id+"F18.wireOp",EDGE,"E22.0");var subQ1=sQuery(id+"F18.wireOp",EDGE,"E22.2");Q10=makeQuery(id+"F21.boolean.opBoolean","SPLIT",EDGE,{"disambiguationData":[TD([makeQuery(id+"F21.opExtrude","SWEPT_FACE",FACE,{"disambiguationData":[OSD([sQuery(id+"F20.wireOp",EDGE,"E24")])]})])],"derivedFrom":makeQuery(id+"F19.opExtrude","SWEPT_EDGE",EDGE,{"disambiguationData":[OSD([subQ0,subQ1])]})});}
            var Q11;
            {var subQ0=sQuery(id+"F18.wireOp",EDGE,"E22.0");var subQ1=sQuery(id+"F18.wireOp",EDGE,"E22.2");Q11=makeQuery(id+"F21.boolean.opBoolean","SPLIT",EDGE,{"disambiguationData":[TD([makeQuery(id+"F21.opExtrude","SWEPT_FACE",FACE,{"disambiguationData":[OSD([sQuery(id+"F20.wireOp",EDGE,"E26")])]})])],"derivedFrom":makeQuery(id+"F19.opExtrude","SWEPT_EDGE",EDGE,{"disambiguationData":[OSD([subQ0,subQ1])]})});}
            var Q12;
            Q12=makeQuery(id+"F19.opExtrude","CAP_EDGE",EDGE,{"disambiguationData":[OSD([sQuery(id+"F18.wireOp",EDGE,"E22.2")])],"isStart":true});
            var Q13;
            {var subQ0=sQuery(id+"F18.wireOp",EDGE,"E22.2");var subQ1=sQuery(id+"F18.wireOp",EDGE,"E22.1");Q13=makeQuery(id+"F21.boolean.opBoolean","SPLIT",EDGE,{"disambiguationData":[TD([makeQuery(id+"F21.opExtrude","SWEPT_FACE",FACE,{"disambiguationData":[OSD([sQuery(id+"F20.wireOp",EDGE,"E26")])]})])],"derivedFrom":makeQuery(id+"F19.opExtrude","SWEPT_EDGE",EDGE,{"disambiguationData":[OSD([subQ1,subQ0])]})});}
            var Q14;
            {var subQ0=sQuery(id+"F18.wireOp",EDGE,"E22.11");var subQ1=sQuery(id+"F18.wireOp",EDGE,"E22.8");Q14=makeQuery(id+"F27.boolean.opBoolean","SPLIT",EDGE,{"disambiguationData":[TD([makeQuery(id+"F27.opExtrude","SWEPT_FACE",FACE,{"disambiguationData":[OSD([sQuery(id+"F26.wireOp",EDGE,"E37.2")])]})])],"derivedFrom":makeQuery(id+"F19.opExtrude","SWEPT_EDGE",EDGE,{"disambiguationData":[OSD([subQ1,subQ0])]})});}
            var Q15;
            Q15=makeQuery(id+"F19.opExtrude","CAP_EDGE",EDGE,{"disambiguationData":[OSD([sQuery(id+"F18.wireOp",EDGE,"E22.11")])],"isStart":false});
            var Q16;
            {var subQ0=sQuery(id+"F18.wireOp",EDGE,"E22.11");var subQ1=sQuery(id+"F18.wireOp",EDGE,"E22.7");Q16=makeQuery(id+"F27.boolean.opBoolean","SPLIT",EDGE,{"disambiguationData":[TD([makeQuery(id+"F27.opExtrude","SWEPT_FACE",FACE,{"disambiguationData":[OSD([sQuery(id+"F26.wireOp",EDGE,"E37.2")])]})])],"derivedFrom":makeQuery(id+"F19.opExtrude","SWEPT_EDGE",EDGE,{"disambiguationData":[OSD([subQ1,subQ0])]})});}
            var Q17;
            {var subQ0=sQuery(id+"F18.wireOp",EDGE,"E22.11");var subQ1=sQuery(id+"F18.wireOp",EDGE,"E22.7");Q17=makeQuery(id+"F27.boolean.opBoolean","SPLIT",EDGE,{"disambiguationData":[TD([makeQuery(id+"F27.opExtrude","SWEPT_FACE",FACE,{"disambiguationData":[OSD([sQuery(id+"F26.wireOp",EDGE,"E37.0")])]})])],"derivedFrom":makeQuery(id+"F19.opExtrude","SWEPT_EDGE",EDGE,{"disambiguationData":[OSD([subQ1,subQ0])]})});}
            var Q18;
            Q18=makeQuery(id+"F19.opExtrude","CAP_EDGE",EDGE,{"disambiguationData":[OSD([sQuery(id+"F18.wireOp",EDGE,"E22.11")])],"isStart":true});
            var Q19;
            {var subQ0=sQuery(id+"F18.wireOp",EDGE,"E22.11");var subQ1=sQuery(id+"F18.wireOp",EDGE,"E22.8");Q19=makeQuery(id+"F27.boolean.opBoolean","SPLIT",EDGE,{"disambiguationData":[TD([makeQuery(id+"F27.opExtrude","SWEPT_FACE",FACE,{"disambiguationData":[OSD([sQuery(id+"F26.wireOp",EDGE,"E37.0")])]})])],"derivedFrom":makeQuery(id+"F19.opExtrude","SWEPT_EDGE",EDGE,{"disambiguationData":[OSD([subQ1,subQ0])]})});}
            var Q20;
            {var subQ0=sQuery(id+"F0.wireOp",EDGE,"E0.left");var subQ1=sQuery(id+"F0.wireOp",EDGE,"E0.top");Q20=makeQuery(id+"F16.opPattern","COPY",EDGE,{"derivedFrom":makeQuery(id+"F11.boolean.opBoolean","MERGE",EDGE,{"derivedFrom":[makeQuery(id+"F6.boolean.opBoolean","MERGE",EDGE,{"derivedFrom":[makeQuery(id+"F1.opExtrude","SWEPT_EDGE",EDGE,{"disambiguationData":[OSD([subQ1,subQ0])]}),makeQuery(id+"F6.opExtrude","SWEPT_EDGE",EDGE,{"disambiguationData":[OSD([subQ1,subQ0])]})]}),makeQuery(id+"F11.opExtrude","SWEPT_EDGE",EDGE,{"disambiguationData":[OSD([subQ1,subQ0])]})]}),"instanceName":"1"});}
            var Q21;
            {var subQ0=sQuery(id+"F0.wireOp",EDGE,"E0.left");var subQ1=sQuery(id+"F0.wireOp",EDGE,"E0.bottom");Q21=makeQuery(id+"F16.opPattern","COPY",EDGE,{"derivedFrom":makeQuery(id+"F11.boolean.opBoolean","MERGE",EDGE,{"derivedFrom":[makeQuery(id+"F6.boolean.opBoolean","MERGE",EDGE,{"derivedFrom":[makeQuery(id+"F1.opExtrude","SWEPT_EDGE",EDGE,{"disambiguationData":[OSD([subQ1,subQ0])]}),makeQuery(id+"F6.opExtrude","SWEPT_EDGE",EDGE,{"disambiguationData":[OSD([subQ1,subQ0])]})]}),makeQuery(id+"F11.opExtrude","SWEPT_EDGE",EDGE,{"disambiguationData":[OSD([subQ1,subQ0])]})]}),"instanceName":"1"});}
            var Q22;
            Q22=makeQuery(id+"F16.opPattern","COPY",EDGE,{"derivedFrom":makeQuery(id+"F1.opExtrude","CAP_EDGE",EDGE,{"disambiguationData":[OSD([sQuery(id+"F0.wireOp",EDGE,"E0.bottom")])],"isStart":false}),"instanceName":"1"});
            var Q23;
            {var subQ0=sQuery(id+"F0.wireOp",EDGE,"E0.bottom");var subQ1=sQuery(id+"F0.wireOp",EDGE,"E0.right");Q23=makeQuery(id+"F16.opPattern","COPY",EDGE,{"derivedFrom":makeQuery(id+"F5.boolean.opBoolean","SPLIT",EDGE,{"disambiguationData":[TD([makeQuery(id+"F1.opExtrude","SWEPT_FACE",FACE,{"disambiguationData":[OSD([subQ0])]})])],"derivedFrom":makeQuery(id+"F1.opExtrude","CAP_EDGE",EDGE,{"disambiguationData":[OSD([subQ1])],"isStart":false})}),"instanceName":"1"});}
            var Q24;
            {var subQ0=sQuery(id+"F0.wireOp",EDGE,"E0.bottom");var subQ1=sQuery(id+"F0.wireOp",EDGE,"E0.left");Q24=makeQuery(id+"F16.opPattern","COPY",EDGE,{"derivedFrom":makeQuery(id+"F5.boolean.opBoolean","SPLIT",EDGE,{"disambiguationData":[TD([makeQuery(id+"F1.opExtrude","SWEPT_FACE",FACE,{"disambiguationData":[OSD([subQ0])]})])],"derivedFrom":makeQuery(id+"F1.opExtrude","CAP_EDGE",EDGE,{"disambiguationData":[OSD([subQ1])],"isStart":false})}),"instanceName":"1"});}
            var Q25;
            {var subQ0=sQuery(id+"F0.wireOp",EDGE,"E0.left");var subQ1=sQuery(id+"F0.wireOp",EDGE,"E0.top");Q25=makeQuery(id+"F16.opPattern","COPY",EDGE,{"derivedFrom":makeQuery(id+"F5.boolean.opBoolean","SPLIT",EDGE,{"disambiguationData":[TD([makeQuery(id+"F1.opExtrude","SWEPT_FACE",FACE,{"disambiguationData":[OSD([subQ1])]})])],"derivedFrom":makeQuery(id+"F1.opExtrude","CAP_EDGE",EDGE,{"disambiguationData":[OSD([subQ0])],"isStart":false})}),"instanceName":"1"});}
            var Q26;
            {var subQ0=sQuery(id+"F0.wireOp",EDGE,"E0.right");var subQ1=sQuery(id+"F0.wireOp",EDGE,"E0.top");Q26=makeQuery(id+"F16.opPattern","COPY",EDGE,{"derivedFrom":makeQuery(id+"F5.boolean.opBoolean","SPLIT",EDGE,{"disambiguationData":[TD([makeQuery(id+"F1.opExtrude","SWEPT_FACE",FACE,{"disambiguationData":[OSD([subQ1])]})])],"derivedFrom":makeQuery(id+"F1.opExtrude","CAP_EDGE",EDGE,{"disambiguationData":[OSD([subQ0])],"isStart":false})}),"instanceName":"1"});}
            var Q27;
            Q27=makeQuery(id+"F16.opPattern","COPY",EDGE,{"derivedFrom":makeQuery(id+"F1.opExtrude","CAP_EDGE",EDGE,{"disambiguationData":[OSD([sQuery(id+"F0.wireOp",EDGE,"E0.top")])],"isStart":false}),"instanceName":"1"});
            var Q28;
            {var subQ0=sQuery(id+"F0.wireOp",EDGE,"E0.right");var subQ1=sQuery(id+"F0.wireOp",EDGE,"E0.top");Q28=makeQuery(id+"F16.opPattern","COPY",EDGE,{"derivedFrom":makeQuery(id+"F6.boolean.opBoolean","MERGE",EDGE,{"derivedFrom":[makeQuery(id+"F1.opExtrude","SWEPT_EDGE",EDGE,{"disambiguationData":[OSD([subQ1,subQ0])]}),makeQuery(id+"F6.opExtrude","SWEPT_EDGE",EDGE,{"disambiguationData":[OSD([subQ1,subQ0])]})]}),"instanceName":"1"});}
            var Q29;
            {var subQ0=sQuery(id+"F0.wireOp",EDGE,"E0.right");var subQ1=sQuery(id+"F0.wireOp",EDGE,"E0.bottom");Q29=makeQuery(id+"F16.opPattern","COPY",EDGE,{"derivedFrom":makeQuery(id+"F6.boolean.opBoolean","MERGE",EDGE,{"derivedFrom":[makeQuery(id+"F1.opExtrude","SWEPT_EDGE",EDGE,{"disambiguationData":[OSD([subQ1,subQ0])]}),makeQuery(id+"F6.opExtrude","SWEPT_EDGE",EDGE,{"disambiguationData":[OSD([subQ1,subQ0])]})]}),"instanceName":"1"});}
            var Q30;
            {var subQ0=sQuery(id+"F0.wireOp",EDGE,"E0.right");var subQ1=sQuery(id+"F0.wireOp",EDGE,"E0.bottom");Q30=makeQuery(id+"F6.boolean.opBoolean","MERGE",EDGE,{"derivedFrom":[makeQuery(id+"F1.opExtrude","SWEPT_EDGE",EDGE,{"disambiguationData":[OSD([subQ1,subQ0])]}),makeQuery(id+"F6.opExtrude","SWEPT_EDGE",EDGE,{"disambiguationData":[OSD([subQ1,subQ0])]})]});}
            var Q31;
            {var subQ0=sQuery(id+"F0.wireOp",EDGE,"E0.right");var subQ1=sQuery(id+"F0.wireOp",EDGE,"E0.top");Q31=makeQuery(id+"F6.boolean.opBoolean","MERGE",EDGE,{"derivedFrom":[makeQuery(id+"F1.opExtrude","SWEPT_EDGE",EDGE,{"disambiguationData":[OSD([subQ1,subQ0])]}),makeQuery(id+"F6.opExtrude","SWEPT_EDGE",EDGE,{"disambiguationData":[OSD([subQ1,subQ0])]})]});}
            var Q32;
            {var subQ0=sQuery(id+"F0.wireOp",EDGE,"E0.left");var subQ1=sQuery(id+"F0.wireOp",EDGE,"E0.top");Q32=makeQuery(id+"F5.boolean.opBoolean","SPLIT",EDGE,{"disambiguationData":[TD([makeQuery(id+"F1.opExtrude","SWEPT_FACE",FACE,{"disambiguationData":[OSD([subQ1])]})])],"derivedFrom":makeQuery(id+"F1.opExtrude","CAP_EDGE",EDGE,{"disambiguationData":[OSD([subQ0])],"isStart":false})});}
            var Q33;
            Q33=makeQuery(id+"F1.opExtrude","CAP_EDGE",EDGE,{"disambiguationData":[OSD([sQuery(id+"F0.wireOp",EDGE,"E0.top")])],"isStart":false});
            var Q34;
            {var subQ0=sQuery(id+"F0.wireOp",EDGE,"E0.right");var subQ1=sQuery(id+"F0.wireOp",EDGE,"E0.top");Q34=makeQuery(id+"F5.boolean.opBoolean","SPLIT",EDGE,{"disambiguationData":[TD([makeQuery(id+"F1.opExtrude","SWEPT_FACE",FACE,{"disambiguationData":[OSD([subQ1])]})])],"derivedFrom":makeQuery(id+"F1.opExtrude","CAP_EDGE",EDGE,{"disambiguationData":[OSD([subQ0])],"isStart":false})});}
            var Q35;
            {var subQ0=sQuery(id+"F0.wireOp",EDGE,"E0.bottom");var subQ1=sQuery(id+"F0.wireOp",EDGE,"E0.right");Q35=makeQuery(id+"F5.boolean.opBoolean","SPLIT",EDGE,{"disambiguationData":[TD([makeQuery(id+"F1.opExtrude","SWEPT_FACE",FACE,{"disambiguationData":[OSD([subQ0])]})])],"derivedFrom":makeQuery(id+"F1.opExtrude","CAP_EDGE",EDGE,{"disambiguationData":[OSD([subQ1])],"isStart":false})});}
            var Q36;
            Q36=makeQuery(id+"F1.opExtrude","CAP_EDGE",EDGE,{"disambiguationData":[OSD([sQuery(id+"F0.wireOp",EDGE,"E0.bottom")])],"isStart":false});
            var Q37;
            {var subQ0=sQuery(id+"F0.wireOp",EDGE,"E0.bottom");var subQ1=sQuery(id+"F0.wireOp",EDGE,"E0.left");Q37=makeQuery(id+"F5.boolean.opBoolean","SPLIT",EDGE,{"disambiguationData":[TD([makeQuery(id+"F1.opExtrude","SWEPT_FACE",FACE,{"disambiguationData":[OSD([subQ0])]})])],"derivedFrom":makeQuery(id+"F1.opExtrude","CAP_EDGE",EDGE,{"disambiguationData":[OSD([subQ1])],"isStart":false})});}
            var Q38;
            {var subQ0=sQuery(id+"F0.wireOp",EDGE,"E0.left");var subQ1=sQuery(id+"F0.wireOp",EDGE,"E0.bottom");Q38=makeQuery(id+"F11.boolean.opBoolean","MERGE",EDGE,{"derivedFrom":[makeQuery(id+"F6.boolean.opBoolean","MERGE",EDGE,{"derivedFrom":[makeQuery(id+"F1.opExtrude","SWEPT_EDGE",EDGE,{"disambiguationData":[OSD([subQ1,subQ0])]}),makeQuery(id+"F6.opExtrude","SWEPT_EDGE",EDGE,{"disambiguationData":[OSD([subQ1,subQ0])]})]}),makeQuery(id+"F11.opExtrude","SWEPT_EDGE",EDGE,{"disambiguationData":[OSD([subQ1,subQ0])]})]});}
            var Q39;
            {var subQ0=sQuery(id+"F0.wireOp",EDGE,"E0.left");var subQ1=sQuery(id+"F0.wireOp",EDGE,"E0.top");Q39=makeQuery(id+"F11.boolean.opBoolean","MERGE",EDGE,{"derivedFrom":[makeQuery(id+"F6.boolean.opBoolean","MERGE",EDGE,{"derivedFrom":[makeQuery(id+"F1.opExtrude","SWEPT_EDGE",EDGE,{"disambiguationData":[OSD([subQ1,subQ0])]}),makeQuery(id+"F6.opExtrude","SWEPT_EDGE",EDGE,{"disambiguationData":[OSD([subQ1,subQ0])]})]}),makeQuery(id+"F11.opExtrude","SWEPT_EDGE",EDGE,{"disambiguationData":[OSD([subQ1,subQ0])]})]});}
            fillet(context, id + "F33", {"entities" : qUnion([Q0, Q1, Q2, Q3, Q4, Q5, Q6, Q7, Q8, Q9, Q10, Q11, Q12, Q13, Q14, Q15, Q16, Q17, Q18, Q19, Q20, Q21, Q22, Q23, Q24, Q25, Q26, Q27, Q28, Q29, Q30, Q31, Q32, Q33, Q34, Q35, Q36, Q37, Q38, Q39]), "radius" : 3 * mm, "tangentPropagation" : true, "allowEdgeOverflow" : false});
        }
        {
            var Q0;
            {var subQ0=sQuery(id+"F0.wireOp",EDGE,"E0.right");Q0=makeQuery(id+"F32.boolean.opBoolean","INTERSECT",EDGE,{"derivedFrom":[makeQuery(id+"F16.opPattern","COPY",FACE,{"derivedFrom":makeQuery(id+"F6.boolean.opBoolean","MERGE",FACE,{"derivedFrom":[makeQuery(id+"F1.opExtrude","SWEPT_FACE",FACE,{"disambiguationData":[OSD([subQ0])]}),makeQuery(id+"F6.opExtrude","SWEPT_FACE",FACE,{"disambiguationData":[OSD([subQ0])]})]}),"instanceName":"1"}),makeQuery(id+"F32.opExtrude","SWEPT_FACE",FACE,{"disambiguationData":[OSD([sQuery(id+"F31.wireOp",EDGE,"E50")])]})]});}
            var Q1;
            {var subQ0=sQuery(id+"F0.wireOp",EDGE,"E0.right");Q1=makeQuery(id+"F32.boolean.opBoolean","INTERSECT",EDGE,{"derivedFrom":[makeQuery(id+"F6.boolean.opBoolean","MERGE",FACE,{"derivedFrom":[makeQuery(id+"F1.opExtrude","SWEPT_FACE",FACE,{"disambiguationData":[OSD([subQ0])]}),makeQuery(id+"F6.opExtrude","SWEPT_FACE",FACE,{"disambiguationData":[OSD([subQ0])]})]}),makeQuery(id+"F32.opExtrude","SWEPT_FACE",FACE,{"disambiguationData":[OSD([sQuery(id+"F31.wireOp",EDGE,"E50")])]})]});}
            var Q2;
            Q2=makeQuery(id+"F32.boolean.opBoolean","COPY",EDGE,{"derivedFrom":makeQuery(id+"F32.opExtrude","CAP_EDGE",EDGE,{"disambiguationData":[OSD([sQuery(id+"F31.wireOp",EDGE,"E50")])],"isStart":true})});
            var Q3;
            {var subQ0=sQuery(id+"F0.wireOp",EDGE,"E0.left");Q3=makeQuery(id+"F32.boolean.opBoolean","INTERSECT",EDGE,{"derivedFrom":[makeQuery(id+"F11.boolean.opBoolean","MERGE",FACE,{"derivedFrom":[makeQuery(id+"F6.boolean.opBoolean","MERGE",FACE,{"derivedFrom":[makeQuery(id+"F1.opExtrude","SWEPT_FACE",FACE,{"disambiguationData":[OSD([subQ0])]}),makeQuery(id+"F6.opExtrude","SWEPT_FACE",FACE,{"disambiguationData":[OSD([subQ0])]})]}),makeQuery(id+"F11.opExtrude","SWEPT_FACE",FACE,{"disambiguationData":[OSD([subQ0])]})]}),makeQuery(id+"F32.opExtrude","SWEPT_FACE",FACE,{"disambiguationData":[OSD([sQuery(id+"F31.wireOp",EDGE,"E53")])]})]});}
            var Q4;
            Q4=makeQuery(id+"F32.boolean.opBoolean","INTERSECT",EDGE,{"derivedFrom":[makeQuery(id+"F19.opExtrude","SWEPT_FACE",FACE,{"disambiguationData":[OSD([sQuery(id+"F18.wireOp",EDGE,"E22.0")])]}),makeQuery(id+"F32.opExtrude","SWEPT_FACE",FACE,{"disambiguationData":[OSD([sQuery(id+"F31.wireOp",EDGE,"E44")])]})]});
            var Q5;
            Q5=makeQuery(id+"F32.boolean.opBoolean","INTERSECT",EDGE,{"derivedFrom":[makeQuery(id+"F19.opExtrude","SWEPT_FACE",FACE,{"disambiguationData":[OSD([sQuery(id+"F18.wireOp",EDGE,"E22.7")])]}),makeQuery(id+"F32.opExtrude","SWEPT_FACE",FACE,{"disambiguationData":[OSD([sQuery(id+"F31.wireOp",EDGE,"E47")])]})]});
            var Q6;
            Q6=makeQuery(id+"F32.boolean.opBoolean","COPY",EDGE,{"derivedFrom":makeQuery(id+"F32.opExtrude","CAP_EDGE",EDGE,{"disambiguationData":[OSD([sQuery(id+"F31.wireOp",EDGE,"E47")])],"isStart":true})});
            var Q7;
            Q7=makeQuery(id+"F32.boolean.opBoolean","INTERSECT",EDGE,{"derivedFrom":[makeQuery(id+"F19.opExtrude","SWEPT_FACE",FACE,{"disambiguationData":[OSD([sQuery(id+"F18.wireOp",EDGE,"E22.1")])]}),makeQuery(id+"F32.opExtrude","SWEPT_FACE",FACE,{"disambiguationData":[OSD([sQuery(id+"F31.wireOp",EDGE,"E42")])]})]});
            fillet(context, id + "F34", {"entities" : qUnion([Q0, Q1, Q2, Q3, Q4, Q5, Q6, Q7]), "radius" : 3 * mm, "tangentPropagation" : true, "allowEdgeOverflow" : false});
        }
        {
            var Q0;
            Q0=makeQuery(id+"F19.opExtrude","SWEPT_EDGE",EDGE,{"disambiguationData":[OSD([sQuery(id+"F18.wireOp",EDGE,"E22.6"),sQuery(id+"F18.wireOp",EDGE,"E22.7")])]});
            var Q1;
            Q1=makeQuery(id+"F19.opExtrude","SWEPT_EDGE",EDGE,{"disambiguationData":[OSD([sQuery(id+"F18.wireOp",EDGE,"E22.1"),sQuery(id+"F18.wireOp",EDGE,"E22.6")])]});
            var Q2;
            Q2=makeQuery(id+"F16.opPattern","COPY",EDGE,{"derivedFrom":makeQuery(id+"F6.opExtrude","CAP_EDGE",EDGE,{"disambiguationData":[OSD([sQuery(id+"F0.wireOp",EDGE,"E0.right")])],"isStart":false}),"instanceName":"1"});
            var Q3;
            Q3=makeQuery(id+"F6.opExtrude","CAP_EDGE",EDGE,{"disambiguationData":[OSD([sQuery(id+"F0.wireOp",EDGE,"E0.right")])],"isStart":false});
            fillet(context, id + "F35", {"entities" : qUnion([Q0, Q1, Q2, Q3]), "radius" : 10 * mm, "tangentPropagation" : true, "allowEdgeOverflow" : false});
        }
        {
            var Q0;
            Q0=makeQuery(id+"F19.opExtrude","CAP_EDGE",EDGE,{"disambiguationData":[OSD([sQuery(id+"F18.wireOp",EDGE,"E22.6")])],"isStart":true});
            var Q1;
            {var subQ0=makeQuery(id+"F11.opExtrude","CAP_EDGE",EDGE,{"disambiguationData":[OSD([sQuery(id+"F0.wireOp",EDGE,"E0.bottom"),sQuery(id+"F10.wireOp",EDGE,"E15.top")])],"isStart":true});Q1=makeQuery(id+"F16.boolean.opBoolean","MERGE",EDGE,{"derivedFrom":[subQ0,makeQuery(id+"F16.opPattern","COPY",EDGE,{"derivedFrom":subQ0,"instanceName":"1"})]});}
            var Q2;
            {var subQ0=makeQuery(id+"F11.opExtrude","CAP_EDGE",EDGE,{"disambiguationData":[OSD([sQuery(id+"F0.wireOp",EDGE,"E0.top"),sQuery(id+"F10.wireOp",EDGE,"E15.bottom")])],"isStart":true});Q2=makeQuery(id+"F16.boolean.opBoolean","MERGE",EDGE,{"derivedFrom":[subQ0,makeQuery(id+"F16.opPattern","COPY",EDGE,{"derivedFrom":subQ0,"instanceName":"1"})]});}
            var Q3;
            Q3=makeQuery(id+"F19.opExtrude","CAP_EDGE",EDGE,{"disambiguationData":[OSD([sQuery(id+"F18.wireOp",EDGE,"E22.6")])],"isStart":false});
            fillet(context, id + "F36", {"entities" : qUnion([Q0, Q1, Q2, Q3]), "radius" : 5 * mm, "tangentPropagation" : true, "allowEdgeOverflow" : false});
        }
        {
            var Q0;
            {var subQ0=makeQuery(id+"F11.opExtrude","CAP_EDGE",EDGE,{"disambiguationData":[OSD([sQuery(id+"F0.wireOp",EDGE,"E0.bottom"),sQuery(id+"F10.wireOp",EDGE,"E15.top")])],"isStart":false});Q0=makeQuery(id+"F16.boolean.opBoolean","MERGE",EDGE,{"derivedFrom":[subQ0,makeQuery(id+"F16.opPattern","COPY",EDGE,{"derivedFrom":subQ0,"instanceName":"1"})]});}
            var Q1;
            Q1=makeQuery(id+"F19.opExtrude","CAP_EDGE",EDGE,{"disambiguationData":[OSD([sQuery(id+"F18.wireOp",EDGE,"E22.5")])],"isStart":true});
            chamfer(context, id + "F37", {"entities" : qUnion([Q0, Q1]), "width" : 1 * mm, "tangentPropagation" : true});
        }
    });
